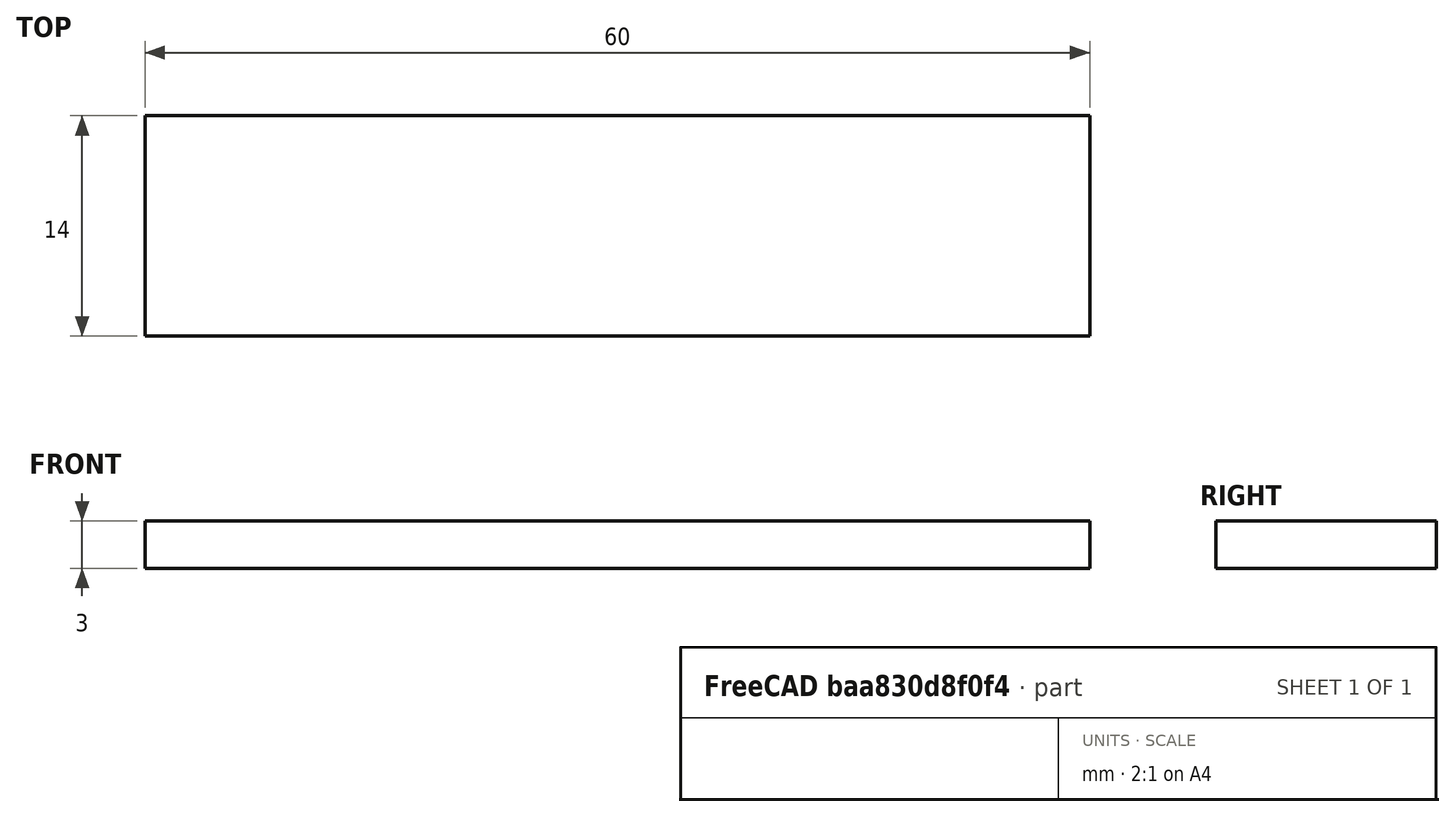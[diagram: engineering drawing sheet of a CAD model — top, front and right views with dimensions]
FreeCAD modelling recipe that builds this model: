
FCSTD DOCUMENT  (FreeCAD 0.17R13541 (Git))
Label: laser_sledge_bar
License: All rights reserved
LicenseURL: http://en.wikipedia.org/wiki/All_rights_reserved
objects: Sketcher::SketchObject×1, PartDesign::Pad×1, PartDesign::Body×1, App::Part×1
note: 4 computed .brp shape members not serialized (recipe doc carries the construction recipe); baked Part::Feature solids carry a one-line shape summary decoded from their .brp

FEATURE [Sketcher::SketchObject] Sketch
  MapMode = 5
  Support = -> [XY_Plane001]
  sketch-geometry (4):
    g0: LineSegment StartX=0 StartY=0 StartZ=0 EndX=60 EndY=0 EndZ=0
    g1: LineSegment StartX=60 StartY=0 StartZ=0 EndX=60 EndY=14 EndZ=0
    g2: LineSegment StartX=60 StartY=14 StartZ=0 EndX=0 EndY=14 EndZ=0
    g3: LineSegment StartX=0 StartY=14 StartZ=0 EndX=0 EndY=0 EndZ=0
  constraints (11):
    c: Coincident(g0,g1)
    c: Coincident(g1,g2)
    c: Coincident(g2,g3)
    c: Coincident(g3,g0)
    c: Horizontal(g0)
    c: Horizontal(g2)
    c: Vertical(g1)
    c: Vertical(g3)
    c: Coincident(g0,g-1)
    c: DistanceX(g2,g2) = 60
    c: DistanceY(g3,g3) = 14
FEATURE [PartDesign::Pad] Pad
  Length = 3
  Length2 = 100
  Profile = -> Sketch
  Type = 0
FEATURE [PartDesign::Body] Body
  Group = -> [Sketch,Pad]
  Origin = -> Origin001
  Tip = -> Pad
FEATURE [App::Part] Part
  Group = -> [Body]
  License = CC BY 3.0
  LicenseURL = http://creativecommons.org/licenses/by/3.0/
  Origin = -> Origin
